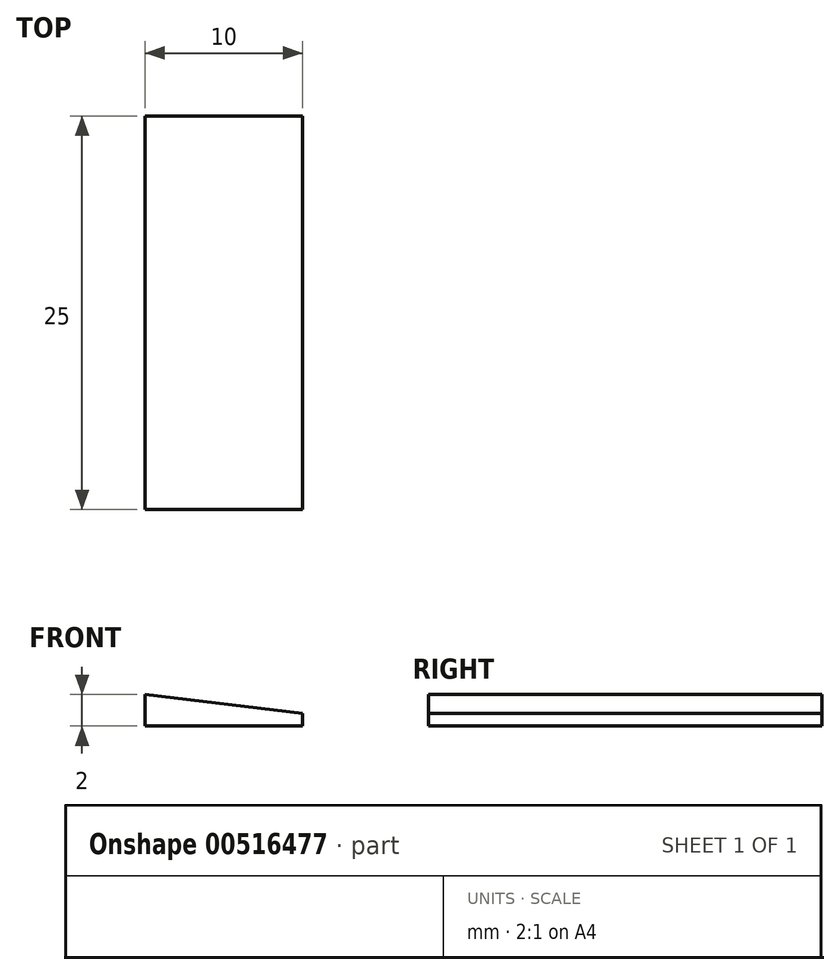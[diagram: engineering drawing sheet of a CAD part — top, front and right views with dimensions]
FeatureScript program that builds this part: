
annotation { "Feature Type Name" : "Feature", "Feature Type Description" : "" }
export const myFeature = defineFeature(function(context is Context, id is Id, definition is map)
    precondition{}
    {
        {
            var Q0;
            Q0=qCreatedBy(makeId("Front.planeOp"),FACE);
            var sketch = newSketch(context, id + "F0", { "sketchPlane" : qUnion([Q0])});
            skLineSegment(sketch, "E0", {"start": v(0, 0) * mm, "end": v(0, 2) * mm});
            skLineSegment(sketch, "E1", {"start": v(0, 2) * mm, "end": v(10, 0.8) * mm});
            skLineSegment(sketch, "E2", {"start": v(10, 0.8) * mm, "end": v(10, 0) * mm});
            skLineSegment(sketch, "E3", {"start": v(10, 0) * mm, "end": v(0, 0) * mm});
            skSolve(sketch);
        }
        {
            var Q0;
            Q0=makeQuery(id+"F0.imprint","IMPRINT",FACE,{"disambiguationData":[TD([[makeQuery(id+"F0.imprint","IMPRINT",EDGE,{"derivedFrom":sQuery(id+"F0.wireOp",EDGE,"E0")}),-1.0]])]});
            extrude(context, id + "F1", {"entities" : qUnion([Q0]), "depth" : 25 * mm, "offsetDistance" : 25 * mm});
        }
    });
